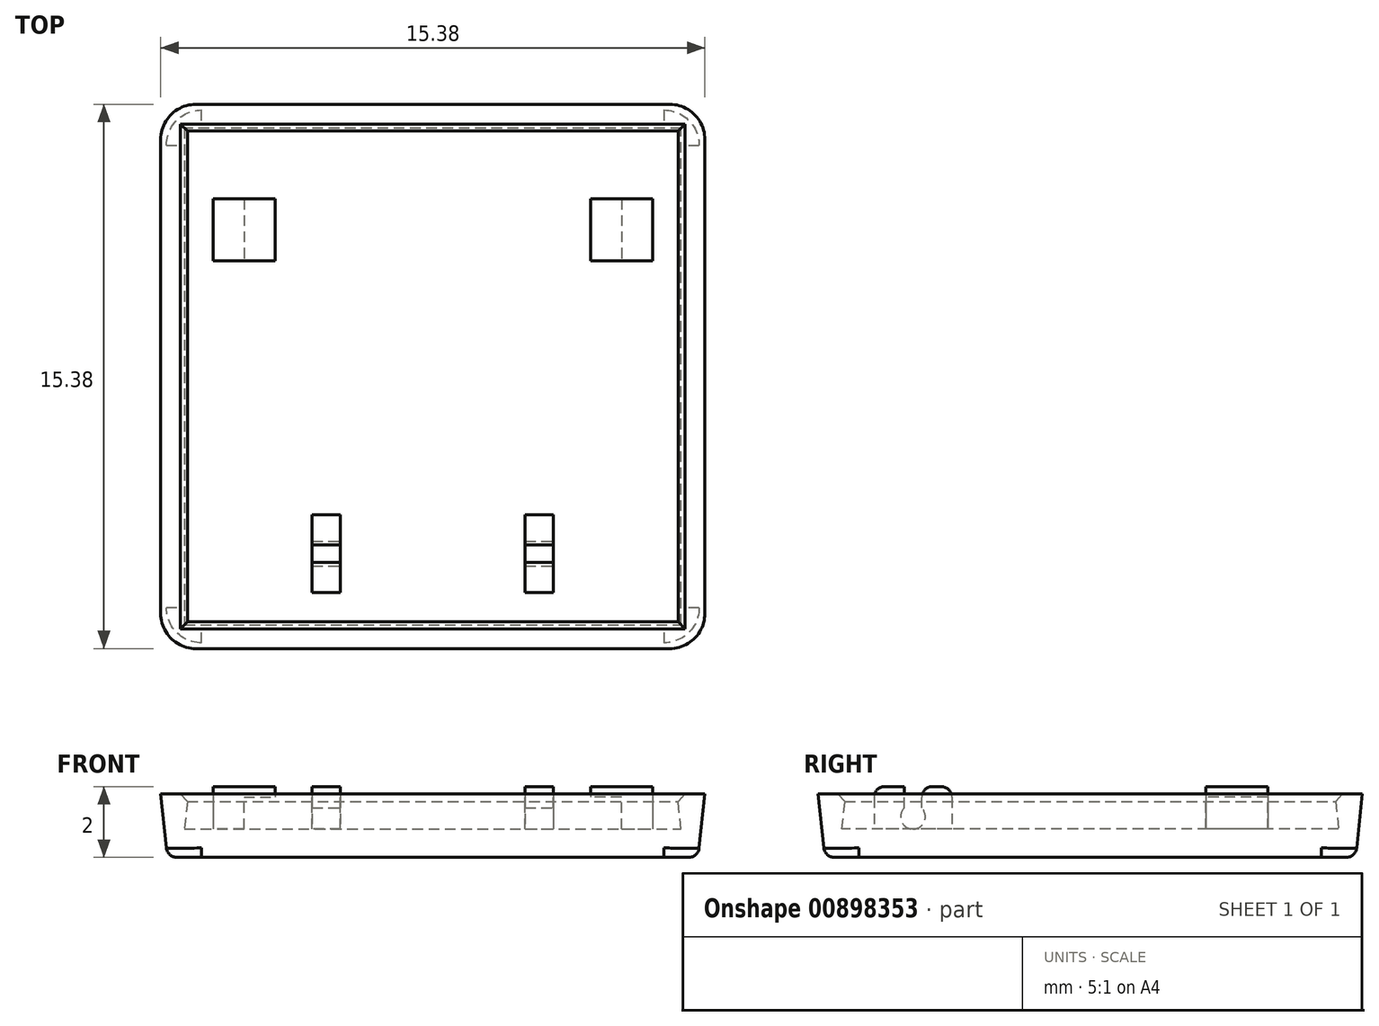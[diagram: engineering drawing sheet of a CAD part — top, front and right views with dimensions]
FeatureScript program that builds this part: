
annotation { "Feature Type Name" : "Feature", "Feature Type Description" : "" }
export const myFeature = defineFeature(function(context is Context, id is Id, definition is map)
    precondition{}
    {
        {
            var Q0;
            Q0=qCreatedBy(makeId("Top.planeOp"),FACE);
            var sketch = newSketch(context, id + "F0", { "sketchPlane" : qUnion([Q0])});
            skLineSegment(sketch, "E0.bottom", {"start": v(0, 0) * mm, "end": v(15, 0) * mm});
            skLineSegment(sketch, "E0.top", {"start": v(0, 15) * mm, "end": v(15, 15) * mm});
            skLineSegment(sketch, "E0.left", {"start": v(0, 0) * mm, "end": v(0, 15) * mm});
            skLineSegment(sketch, "E0.right", {"start": v(15, 0) * mm, "end": v(15, 15) * mm});
            skLineSegment(sketch, "E1.0", {"start": v(0.4, 14.6) * mm, "end": v(14.6, 14.6) * mm});
            skLineSegment(sketch, "E1.1", {"start": v(0.4, 0.4) * mm, "end": v(0.4, 14.6) * mm});
            skLineSegment(sketch, "E1.2", {"start": v(0.4, 0.4) * mm, "end": v(14.6, 0.4) * mm});
            skLineSegment(sketch, "E1.3", {"start": v(14.6, 0.4) * mm, "end": v(14.6, 14.6) * mm});
            skSolve(sketch);
        }
        {
            var Q0;
            Q0=makeQuery(id+"F0.imprint","IMPRINT",FACE,{"disambiguationData":[TD([[makeQuery(id+"F0.imprint","IMPRINT",EDGE,{"derivedFrom":sQuery(id+"F0.wireOp",EDGE,"E0.bottom")}),1.0]])]});
            extrude(context, id + "F1", {"entities" : qUnion([Q0]), "depth" : 1.8 * mm, "offsetDistance" : 25 * mm, "hasDraft" : true, "draftAngle" : 6 * degree});
        }
        {
            var Q0;
            Q0=makeQuery(id+"F0.imprint","IMPRINT",FACE,{"disambiguationData":[TD([[makeQuery(id+"F0.imprint","IMPRINT",EDGE,{"derivedFrom":sQuery(id+"F0.wireOp",EDGE,"E1.0")}),-1.0]])]});
            extrude(context, id + "F2", {"entities" : qUnion([Q0]), "operationType" : NewBodyOperationType.ADD, "depth" : .8 * mm, "offsetDistance" : 25 * mm});
        }
        {
            var Q0;
            {var subQ0=sQuery(id+"F0.wireOp",EDGE,"E1.3");var subQ1=sQuery(id+"F0.wireOp",EDGE,"E1.2");var subQ2=sQuery(id+"F0.wireOp",EDGE,"E1.1");var subQ3=sQuery(id+"F0.wireOp",EDGE,"E1.0");Q0=makeQuery(id+"F2.boolean.opBoolean","MERGE",FACE,{"derivedFrom":[makeQuery(id+"F1.opExtrude","CAP_FACE",FACE,{"disambiguationData":[OSD([sQuery(id+"F0.wireOp",EDGE,"E0.bottom"),sQuery(id+"F0.wireOp",EDGE,"E0.top"),sQuery(id+"F0.wireOp",EDGE,"E0.left"),sQuery(id+"F0.wireOp",EDGE,"E0.right"),subQ3,subQ2,subQ1,subQ0])],"isStart":true}),makeQuery(id+"F2.opExtrude","CAP_FACE",FACE,{"disambiguationData":[OSD([subQ3,subQ2,subQ1,subQ0])],"isStart":true})]});}
            fillet(context, id + "F3", {"entities" : qUnion([Q0]), "radius" : .3 * mm, "tangentPropagation" : true, "allowEdgeOverflow" : false});
        }
        {
            var Q0;
            Q0=makeQuery(id+"F1.opExtrude","SWEPT_EDGE",EDGE,{"disambiguationData":[OSD([sQuery(id+"F0.wireOp",EDGE,"E0.top"),sQuery(id+"F0.wireOp",EDGE,"E0.left")])]});
            var Q1;
            Q1=makeQuery(id+"F1.opExtrude","SWEPT_EDGE",EDGE,{"disambiguationData":[OSD([sQuery(id+"F0.wireOp",EDGE,"E0.bottom"),sQuery(id+"F0.wireOp",EDGE,"E0.left")])]});
            var Q2;
            Q2=makeQuery(id+"F1.opExtrude","SWEPT_EDGE",EDGE,{"disambiguationData":[OSD([sQuery(id+"F0.wireOp",EDGE,"E0.bottom"),sQuery(id+"F0.wireOp",EDGE,"E0.right")])]});
            var Q3;
            Q3=makeQuery(id+"F1.opExtrude","SWEPT_EDGE",EDGE,{"disambiguationData":[OSD([sQuery(id+"F0.wireOp",EDGE,"E0.top"),sQuery(id+"F0.wireOp",EDGE,"E0.right")])]});
            fillet(context, id + "F4", {"entities" : qUnion([Q0, Q1, Q2, Q3]), "radius" : 1 * mm, "tangentPropagation" : true, "allowEdgeOverflow" : false});
        }
        {
            var Q0;
            Q0=makeQuery(id+"F2.opExtrude","CAP_FACE",FACE,{"disambiguationData":[OSD([sQuery(id+"F0.wireOp",EDGE,"E1.0"),sQuery(id+"F0.wireOp",EDGE,"E1.1"),sQuery(id+"F0.wireOp",EDGE,"E1.2"),sQuery(id+"F0.wireOp",EDGE,"E1.3")])],"isStart":false});
            var sketch = newSketch(context, id + "F5", { "sketchPlane" : qUnion([Q0])});
            skLineSegment(sketch, "E2", {"start": v(7.5, 14.52) * mm, "end": v(7.5, -5) * mm, "construction": true});
            skLineSegment(sketch, "E3.bottom", {"start": v(10.11, 3.59) * mm, "end": v(10.91, 3.59) * mm});
            skLineSegment(sketch, "E3.top", {"start": v(10.11, 1.39) * mm, "end": v(10.91, 1.39) * mm});
            skLineSegment(sketch, "E3.left", {"start": v(10.11, 3.59) * mm, "end": v(10.11, 1.39) * mm});
            skLineSegment(sketch, "E3.right", {"start": v(10.91, 3.59) * mm, "end": v(10.91, 1.39) * mm});
            skLineSegment(sketch, "E4.MirrorCS", {"start": v(4.89, 3.59) * mm, "end": v(4.09, 3.59) * mm});
            skLineSegment(sketch, "E5.MirrorCS", {"start": v(4.89, 1.39) * mm, "end": v(4.09, 1.39) * mm});
            skLineSegment(sketch, "E6.MirrorCS", {"start": v(4.09, 3.59) * mm, "end": v(4.09, 1.39) * mm});
            skLineSegment(sketch, "E7.MirrorCS", {"start": v(4.89, 3.59) * mm, "end": v(4.89, 1.39) * mm});
            skLineSegment(sketch, "E8.bottom", {"start": v(11.96, 12.52) * mm, "end": v(13.71, 12.52) * mm});
            skLineSegment(sketch, "E8.top", {"start": v(11.96, 10.77) * mm, "end": v(13.71, 10.77) * mm});
            skLineSegment(sketch, "E8.left", {"start": v(11.96, 12.52) * mm, "end": v(11.96, 10.77) * mm});
            skLineSegment(sketch, "E8.right", {"start": v(13.71, 12.52) * mm, "end": v(13.71, 10.77) * mm});
            skLineSegment(sketch, "E9.MirrorCS", {"start": v(3.04, 12.52) * mm, "end": v(1.29, 12.52) * mm});
            skLineSegment(sketch, "E10.MirrorCS", {"start": v(3.04, 10.77) * mm, "end": v(1.29, 10.77) * mm});
            skLineSegment(sketch, "E11.MirrorCS", {"start": v(3.04, 12.52) * mm, "end": v(3.04, 10.77) * mm});
            skLineSegment(sketch, "E12.MirrorCS", {"start": v(1.29, 12.52) * mm, "end": v(1.29, 10.77) * mm});
            skSolve(sketch);
        }
        {
            var Q0;
            Q0 = qSketchRegion(id + "F5", true);
            extrude(context, id + "F6", {"entities" : qUnion([Q0]), "operationType" : NewBodyOperationType.ADD, "depth" : 1.2 * mm, "offsetDistance" : 25 * mm});
        }
        {
            var Q0;
            Q0=makeQuery(id+"F6.opExtrude","SWEPT_FACE",FACE,{"disambiguationData":[OSD([sQuery(id+"F5.wireOp",EDGE,"E3.right")])]});
            var sketch = newSketch(context, id + "F7", { "sketchPlane" : qUnion([Q0])});
            skArc(sketch, "E13", {"start": v(2.24, 1.4) * mm, "mid": v(2.49, 0.8) * mm, "end": v(2.74, 1.4) * mm});
            skPoint(sketch, "E13.centerSnap0", {"position": v(2.49, 0.8) * mm});
            skLineSegment(sketch, "E14", {"start": v(2.74, 1.4) * mm, "end": v(2.74, 2) * mm});
            skLineSegment(sketch, "E15", {"start": v(2.24, 1.4) * mm, "end": v(2.24, 2) * mm});
            skLineSegment(sketch, "E16", {"start": v(2.74, 2) * mm, "end": v(2.24, 2) * mm});
            skSolve(sketch);
        }
        {
            var Q0;
            Q0 = qSketchRegion(id + "F7", true);
            extrude(context, id + "F8", {"entities" : qUnion([Q0]), "operationType" : NewBodyOperationType.REMOVE, "oppositeDirection" : true, "depth" : 8.47 * mm, "offsetDistance" : 25 * mm});
        }
        {
            var Q0;
            Q0=makeQuery(id+"F6.opExtrude","CAP_EDGE",EDGE,{"disambiguationData":[OSD([sQuery(id+"F5.wireOp",EDGE,"E4.MirrorCS")])],"isStart":false});
            var Q1;
            Q1=makeQuery(id+"F6.opExtrude","CAP_EDGE",EDGE,{"disambiguationData":[OSD([sQuery(id+"F5.wireOp",EDGE,"E5.MirrorCS")])],"isStart":false});
            var Q2;
            Q2=makeQuery(id+"F6.opExtrude","CAP_EDGE",EDGE,{"disambiguationData":[OSD([sQuery(id+"F5.wireOp",EDGE,"E3.top")])],"isStart":false});
            var Q3;
            Q3=makeQuery(id+"F6.opExtrude","CAP_EDGE",EDGE,{"disambiguationData":[OSD([sQuery(id+"F5.wireOp",EDGE,"E3.bottom")])],"isStart":false});
            var Q4;
            {var subQ0=sQuery(id+"F7.wireOp",EDGE,"E14");Q4=makeQuery(id+"F8.boolean.opBoolean","COPY",EDGE,{"disambiguationData":[topologyDisambiguationEdgeConnected([makeQuery(id+"F6.opExtrude","CAP_FACE",FACE,{"disambiguationData":[OSD([sQuery(id+"F5.wireOp",EDGE,"E4.MirrorCS"),sQuery(id+"F5.wireOp",EDGE,"E5.MirrorCS"),sQuery(id+"F5.wireOp",EDGE,"E6.MirrorCS"),sQuery(id+"F5.wireOp",EDGE,"E7.MirrorCS")])],"isStart":false})])],"derivedFrom":makeQuery(id+"F8.opExtrude","SWEPT_EDGE",EDGE,{"disambiguationData":[OSD([sQuery(id+"F5.wireOp",EDGE,"E3.right"),subQ0,sQuery(id+"F7.wireOp",EDGE,"E16")])]})});}
            var Q5;
            {var subQ0=sQuery(id+"F7.wireOp",EDGE,"E15");Q5=makeQuery(id+"F8.boolean.opBoolean","COPY",EDGE,{"disambiguationData":[topologyDisambiguationEdgeConnected([makeQuery(id+"F6.opExtrude","CAP_FACE",FACE,{"disambiguationData":[OSD([sQuery(id+"F5.wireOp",EDGE,"E4.MirrorCS"),sQuery(id+"F5.wireOp",EDGE,"E5.MirrorCS"),sQuery(id+"F5.wireOp",EDGE,"E6.MirrorCS"),sQuery(id+"F5.wireOp",EDGE,"E7.MirrorCS")])],"isStart":false})])],"derivedFrom":makeQuery(id+"F8.opExtrude","SWEPT_EDGE",EDGE,{"disambiguationData":[OSD([sQuery(id+"F5.wireOp",EDGE,"E3.right"),subQ0,sQuery(id+"F7.wireOp",EDGE,"E16")])]})});}
            var Q6;
            {var subQ0=sQuery(id+"F5.wireOp",EDGE,"E3.right");var subQ1=sQuery(id+"F7.wireOp",EDGE,"E15");Q6=makeQuery(id+"F8.boolean.opBoolean","COPY",EDGE,{"disambiguationData":[topologyDisambiguationEdgeConnected([makeQuery(id+"F6.opExtrude","CAP_FACE",FACE,{"disambiguationData":[OSD([sQuery(id+"F5.wireOp",EDGE,"E3.bottom"),sQuery(id+"F5.wireOp",EDGE,"E3.top"),sQuery(id+"F5.wireOp",EDGE,"E3.left"),subQ0])],"isStart":false})])],"derivedFrom":makeQuery(id+"F8.opExtrude","SWEPT_EDGE",EDGE,{"disambiguationData":[OSD([subQ0,subQ1,sQuery(id+"F7.wireOp",EDGE,"E16")])]})});}
            var Q7;
            {var subQ0=sQuery(id+"F5.wireOp",EDGE,"E3.right");var subQ1=sQuery(id+"F7.wireOp",EDGE,"E14");Q7=makeQuery(id+"F8.boolean.opBoolean","COPY",EDGE,{"disambiguationData":[topologyDisambiguationEdgeConnected([makeQuery(id+"F6.opExtrude","CAP_FACE",FACE,{"disambiguationData":[OSD([sQuery(id+"F5.wireOp",EDGE,"E3.bottom"),sQuery(id+"F5.wireOp",EDGE,"E3.top"),sQuery(id+"F5.wireOp",EDGE,"E3.left"),subQ0])],"isStart":false})])],"derivedFrom":makeQuery(id+"F8.opExtrude","SWEPT_EDGE",EDGE,{"disambiguationData":[OSD([subQ0,subQ1,sQuery(id+"F7.wireOp",EDGE,"E16")])]})});}
            fillet(context, id + "F9", {"entities" : qUnion([Q0, Q1, Q2, Q3, Q4, Q5, Q6, Q7]), "radius" : .3 * mm, "tangentPropagation" : true, "allowEdgeOverflow" : false});
        }
        {
            var Q0;
            Q0=makeQuery(id+"F1.opExtrude","CAP_EDGE",EDGE,{"disambiguationData":[OSD([sQuery(id+"F0.wireOp",EDGE,"E1.0")])],"isStart":false});
            var Q1;
            Q1=makeQuery(id+"F1.opExtrude","CAP_EDGE",EDGE,{"disambiguationData":[OSD([sQuery(id+"F0.wireOp",EDGE,"E1.1")])],"isStart":false});
            var Q2;
            Q2=makeQuery(id+"F1.opExtrude","CAP_EDGE",EDGE,{"disambiguationData":[OSD([sQuery(id+"F0.wireOp",EDGE,"E1.2")])],"isStart":false});
            var Q3;
            Q3=makeQuery(id+"F1.opExtrude","CAP_EDGE",EDGE,{"disambiguationData":[OSD([sQuery(id+"F0.wireOp",EDGE,"E1.3")])],"isStart":false});
            chamfer(context, id + "F10", {"entities" : qUnion([Q0, Q1, Q2, Q3]), "width" : .2 * mm, "tangentPropagation" : true});
        }
        {
            var Q0;
            Q0=makeQuery(id+"F6.opExtrude","SWEPT_FACE",FACE,{"disambiguationData":[OSD([sQuery(id+"F5.wireOp",EDGE,"E8.top")])]});
            var sketch = newSketch(context, id + "F11", { "sketchPlane" : qUnion([Q0])});
            skLineSegment(sketch, "E17", {"start": v(12.84, 0.8) * mm, "end": v(12.84, 1.7) * mm});
            skLineSegment(sketch, "E18", {"start": v(12.84, 1.7) * mm, "end": v(11.96, 1.7) * mm});
            skLineSegment(sketch, "E19", {"start": v(11.96, 1.7) * mm, "end": v(11.96, 0.8) * mm});
            skLineSegment(sketch, "E20", {"start": v(11.96, 0.8) * mm, "end": v(12.84, 0.8) * mm});
            skSolve(sketch);
        }
        {
            var Q0;
            Q0 = qSketchRegion(id + "F11", true);
            extrude(context, id + "F12", {"entities" : qUnion([Q0]), "operationType" : NewBodyOperationType.REMOVE, "oppositeDirection" : true, "depth" : 2 * mm, "offsetDistance" : 25 * mm});
        }
        {
            var Q0;
            Q0=makeQuery(id+"F6.opExtrude","SWEPT_FACE",FACE,{"disambiguationData":[OSD([sQuery(id+"F5.wireOp",EDGE,"E10.MirrorCS")])]});
            var sketch = newSketch(context, id + "F13", { "sketchPlane" : qUnion([Q0])});
            skLineSegment(sketch, "E21", {"start": v(2.16, 0.8) * mm, "end": v(2.16, 1.7) * mm});
            skLineSegment(sketch, "E22", {"start": v(2.16, 1.7) * mm, "end": v(3.04, 1.7) * mm});
            skLineSegment(sketch, "E23", {"start": v(3.04, 1.7) * mm, "end": v(3.04, 0.8) * mm});
            skLineSegment(sketch, "E24", {"start": v(3.04, 0.8) * mm, "end": v(2.16, 0.8) * mm});
            skSolve(sketch);
        }
        {
            var Q0;
            Q0 = qSketchRegion(id + "F13", true);
            extrude(context, id + "F14", {"entities" : qUnion([Q0]), "operationType" : NewBodyOperationType.REMOVE, "oppositeDirection" : true, "depth" : 2 * mm, "offsetDistance" : 25 * mm});
        }
    });
